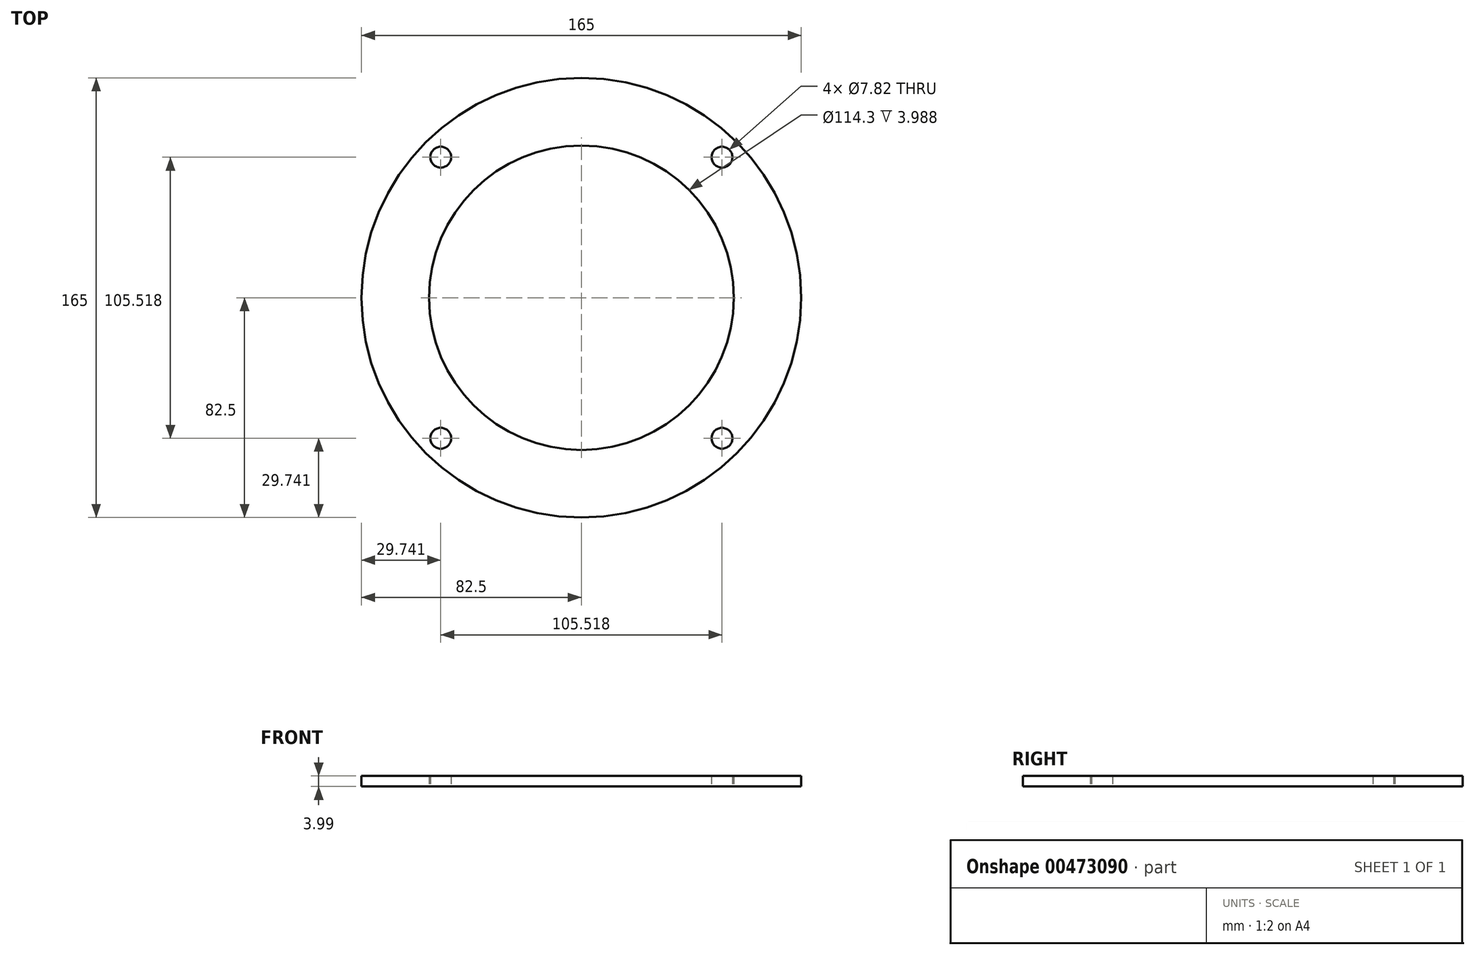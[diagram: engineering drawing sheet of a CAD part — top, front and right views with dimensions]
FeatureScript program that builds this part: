
annotation { "Feature Type Name" : "Feature", "Feature Type Description" : "" }
export const myFeature = defineFeature(function(context is Context, id is Id, definition is map)
    precondition{}
    {
        {
            var Q0;
            Q0=qCreatedBy(makeId("Top.planeOp"),FACE);
            var sketch = newSketch(context, id + "F0", { "sketchPlane" : qUnion([Q0])});
            skCircle(sketch, "E0", {"center": v(0, 0) * mm, "radius": 82.5 * mm});
            skCircle(sketch, "E1", {"center": v(0, 0) * mm, "radius": 57.15 * mm});
            skCircle(sketch, "E2", {"center": v(0, 0) * mm, "radius": 74.61 * mm, "construction": true});
            skCircle(sketch, "E3", {"center": v(-52.76, 52.76) * mm, "radius": 3.9 * mm});
            skCircle(sketch, "E4", {"center": v(52.76, 52.76) * mm, "radius": 3.9 * mm});
            skCircle(sketch, "E5", {"center": v(52.76, -52.76) * mm, "radius": 3.9 * mm});
            skCircle(sketch, "E6", {"center": v(-52.76, -52.76) * mm, "radius": 3.9 * mm});
            skLineSegment(sketch, "E7", {"start": v(-52.76, 52.76) * mm, "end": v(-52.76, -52.76) * mm, "construction": true});
            skLineSegment(sketch, "E8", {"start": v(52.76, -52.76) * mm, "end": v(-52.76, -52.76) * mm, "construction": true});
            skSolve(sketch);
        }
        {
            var Q0;
            Q0 = qSketchRegion(id + "F0", true);
            extrude(context, id + "F1", {"entities" : qUnion([Q0]), "depth" : 4 * mm});
        }
    });
